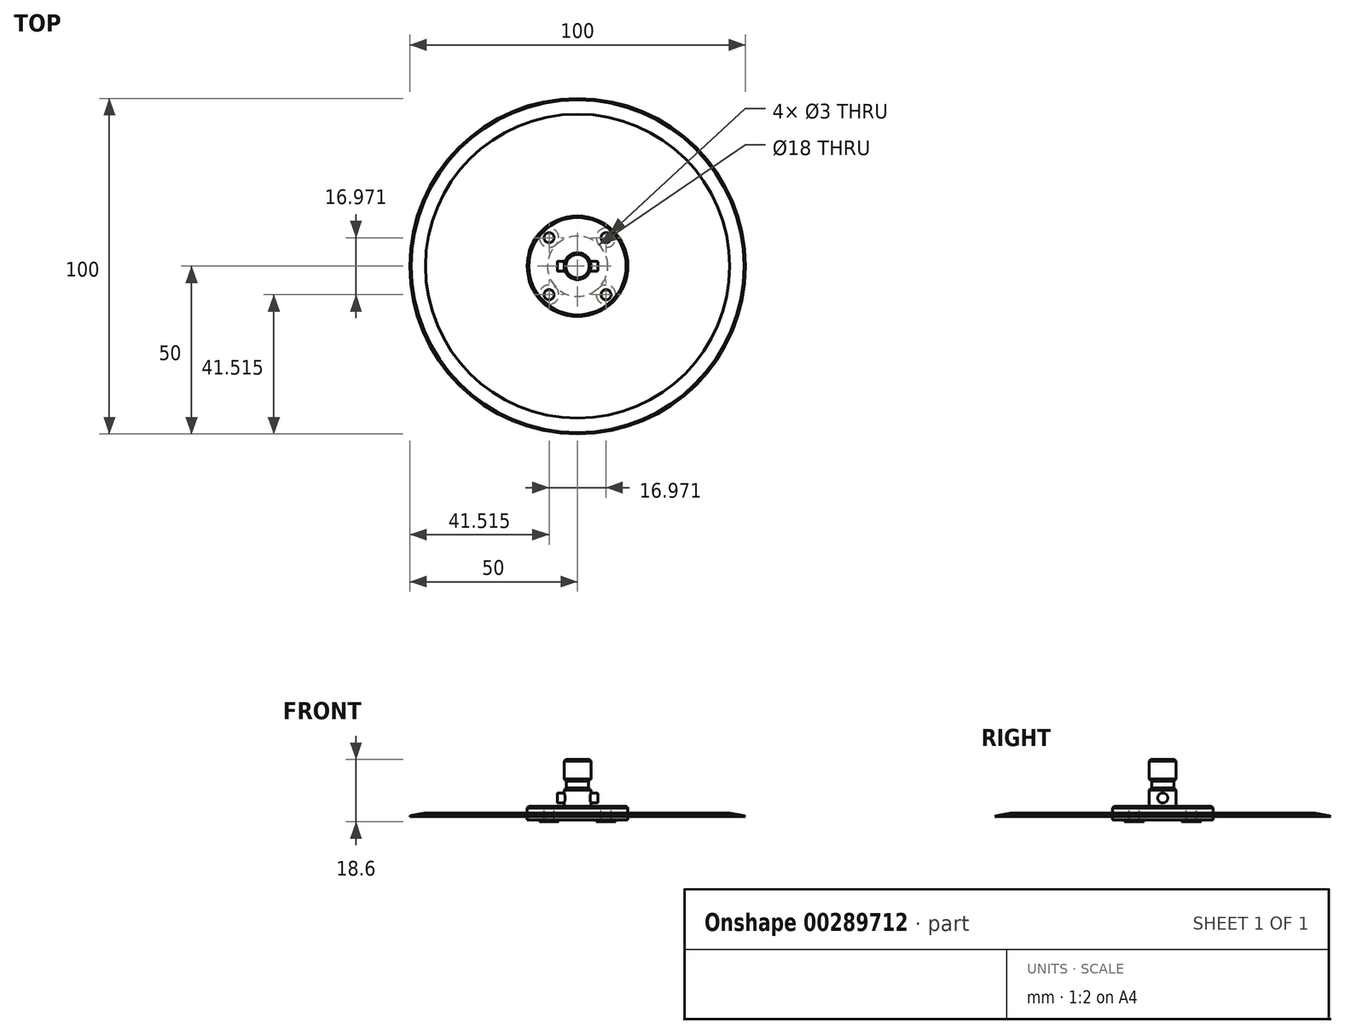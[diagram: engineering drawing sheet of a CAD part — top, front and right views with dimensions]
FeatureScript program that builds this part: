
annotation { "Feature Type Name" : "Feature", "Feature Type Description" : "" }
export const myFeature = defineFeature(function(context is Context, id is Id, definition is map)
    precondition{}
    {
        {
            var Q0;
            Q0=qCreatedBy(makeId("Top.planeOp"),FACE);
            var sketch = newSketch(context, id + "F0", { "sketchPlane" : qUnion([Q0])});
            skCircle(sketch, "E0", {"center": v(0, 0) * mm, "radius": 50 * mm});
            skCircle(sketch, "E1", {"center": v(0, 0) * mm, "radius": 9 * mm});
            skCircle(sketch, "E2", {"center": v(-8.49, -8.49) * mm, "radius": 1.5 * mm});
            skLineSegment(sketch, "E3", {"start": v(0, 0) * mm, "end": v(-8.49, -8.49) * mm, "construction": true});
            skCircle(sketch, "E4.1.0", {"center": v(8.49, -8.49) * mm, "radius": 1.5 * mm});
            skCircle(sketch, "E4.2.0", {"center": v(8.49, 8.49) * mm, "radius": 1.5 * mm});
            skCircle(sketch, "E4.3.0", {"center": v(-8.49, 8.49) * mm, "radius": 1.5 * mm});
            skSolve(sketch);
        }
        {
            var Q0;
            Q0 = qSketchRegion(id + "F0", true);
            var Q1;
            Q1=makeQuery(id+"F0.imprint","IMPRINT",FACE,{"disambiguationData":[TD([[makeQuery(id+"F0.imprint","IMPRINT",EDGE,{"derivedFrom":sQuery(id+"F0.wireOp",EDGE,"E0")}),1.0]])]});
            extrude(context, id + "F1", {"entities" : qUnion([Q0, Q1]), "depth" : 1 * mm});
        }
        {
            var Q0;
            Q0=qCreatedBy(makeId("Front.planeOp"),FACE);
            var sketch = newSketch(context, id + "F2", { "sketchPlane" : qUnion([Q0])});
            skLineSegment(sketch, "E5.0", {"start": v(-50, 0) * mm, "end": v(50, 0) * mm});
            skLineSegment(sketch, "E6", {"start": v(50, 0) * mm, "end": v(49.57, 0.25) * mm});
            skLineSegment(sketch, "E7", {"start": v(49.57, 0.25) * mm, "end": v(39.36, 2.05) * mm});
            skLineSegment(sketch, "E8", {"start": v(39.36, 2.05) * mm, "end": v(52.74, 3.14) * mm});
            skLineSegment(sketch, "E9", {"start": v(52.74, 3.14) * mm, "end": v(50, 0) * mm});
            skLineSegment(sketch, "E10", {"start": v(0, 0) * mm, "end": v(0, -8.1) * mm});
            skSolve(sketch);
        }
        {
            var Q0;
            Q0=makeQuery(id+"F2.imprint","IMPRINT",FACE,{"disambiguationData":[TD([[makeQuery(id+"F2.imprint","IMPRINT",EDGE,{"derivedFrom":sQuery(id+"F2.wireOp",EDGE,"E6")}),-1.0]])]});
            var Q1;
            Q1=sQuery(id+"F2.wireOp",EDGE,"E10");
            revolve(context, id + "F3", {"operationType" : NewBodyOperationType.REMOVE, "entities" : qUnion([Q0]), "axis" : qUnion([Q1]), "revolveType" : RevolveType.FULL, "oppositeDirection" : true});
        }
        {
            var Q0;
            Q0=qCreatedBy(makeId("Front.planeOp"),FACE);
            var sketch = newSketch(context, id + "F4", { "sketchPlane" : qUnion([Q0])});
            skLineSegment(sketch, "E11", {"start": v(0, -0.82) * mm, "end": v(0, -13.84) * mm, "construction": true});
            skLineSegment(sketch, "E12", {"start": v(0, 17) * mm, "end": v(4, 17) * mm});
            skLineSegment(sketch, "E13", {"start": v(4, 17) * mm, "end": v(4, 10.5) * mm});
            skLineSegment(sketch, "E14", {"start": v(4, 10.5) * mm, "end": v(3.3, 10.5) * mm});
            skLineSegment(sketch, "E15", {"start": v(3.3, 10.5) * mm, "end": v(3.3, 8.5) * mm});
            skLineSegment(sketch, "E16", {"start": v(3.3, 8.5) * mm, "end": v(4, 8.5) * mm});
            skLineSegment(sketch, "E17", {"start": v(4, 8.5) * mm, "end": v(4, 3) * mm});
            skLineSegment(sketch, "E18", {"start": v(4, 3) * mm, "end": v(15, 3) * mm});
            skLineSegment(sketch, "E19.0", {"start": v(-45.31, 1) * mm, "end": v(45.31, 1) * mm, "construction": true});
            skLineSegment(sketch, "E20", {"start": v(15, 3) * mm, "end": v(15, 1) * mm});
            skLineSegment(sketch, "E21.0", {"start": v(-9, 1) * mm, "end": v(9, 1) * mm, "construction": true});
            skLineSegment(sketch, "E22", {"start": v(15, 1) * mm, "end": v(9, 1) * mm});
            skLineSegment(sketch, "E23", {"start": v(9, 1) * mm, "end": v(9, 0) * mm});
            skLineSegment(sketch, "E24", {"start": v(9, 0) * mm, "end": v(0, 0) * mm});
            skLineSegment(sketch, "E25", {"start": v(0, 0) * mm, "end": v(0, 17) * mm});
            skSolve(sketch);
        }
        {
            var Q0;
            Q0=makeQuery(id+"F4.imprint","IMPRINT",FACE,{"disambiguationData":[TD([[makeQuery(id+"F4.imprint","IMPRINT",EDGE,{"derivedFrom":sQuery(id+"F4.wireOp",EDGE,"E12")}),-1.0]])]});
            var Q1;
            Q1=sQuery(id+"F4.wireOp",EDGE,"E11");
            revolve(context, id + "F5", {"entities" : qUnion([Q0]), "axis" : qUnion([Q1]), "revolveType" : RevolveType.FULL});
        }
        {
            var Q0;
            Q0=makeQuery(id+"F5.opRevolve","SWEPT_EDGE",EDGE,{"disambiguationData":[OSD([sQuery(id+"F4.wireOp",EDGE,"E12"),sQuery(id+"F4.wireOp",EDGE,"E13")])]});
            var Q1;
            Q1=makeQuery(id+"F5.opRevolve","SWEPT_EDGE",EDGE,{"disambiguationData":[OSD([sQuery(id+"F4.wireOp",EDGE,"E18"),sQuery(id+"F4.wireOp",EDGE,"E20")])]});
            chamfer(context, id + "F6", {"entities" : qUnion([Q0, Q1]), "width" : 0.5 * mm, "tangentPropagation" : true});
        }
        {
            var Q0;
            Q0=makeQuery(id+"F5.opRevolve","SWEPT_EDGE",EDGE,{"disambiguationData":[OSD([sQuery(id+"F4.wireOp",EDGE,"E16"),sQuery(id+"F4.wireOp",EDGE,"E17")])]});
            var Q1;
            Q1=makeQuery(id+"F5.opRevolve","SWEPT_EDGE",EDGE,{"disambiguationData":[OSD([sQuery(id+"F4.wireOp",EDGE,"E13"),sQuery(id+"F4.wireOp",EDGE,"E14")])]});
            chamfer(context, id + "F7", {"entities" : qUnion([Q0, Q1]), "width" : 0.7 * mm, "tangentPropagation" : true});
        }
        {
            var Q0;
            Q0=makeQuery(id+"F1.opExtrude","CAP_FACE",FACE,{"disambiguationData":[OSD([sQuery(id+"F0.wireOp",EDGE,"E0"),sQuery(id+"F0.wireOp",EDGE,"E1"),sQuery(id+"F0.wireOp",EDGE,"E2"),sQuery(id+"F0.wireOp",EDGE,"E4.1.0"),sQuery(id+"F0.wireOp",EDGE,"E4.2.0"),sQuery(id+"F0.wireOp",EDGE,"E4.3.0")])],"isStart":true});
            var sketch = newSketch(context, id + "F8", { "sketchPlane" : qUnion([Q0])});
            skCircle(sketch, "E26", {"center": v(0, 0) * mm, "radius": 15 * mm});
            skSolve(sketch);
        }
        {
            var Q0;
            Q0 = qSketchRegion(id + "F8", true);
            extrude(context, id + "F9", {"entities" : qUnion([Q0]), "depth" : 1.1 * mm});
        }
        {
            var Q0;
            Q0=qCreatedBy(makeId("Front.planeOp"),FACE);
            var sketch = newSketch(context, id + "F10", { "sketchPlane" : qUnion([Q0])});
            skLineSegment(sketch, "E27", {"start": v(0, 0) * mm, "end": v(0, 41.1) * mm});
            skSolve(sketch);
        }
        {
            var Q0;
            Q0=qCreatedBy(makeId("Front.planeOp"),FACE);
            var Q1;
            Q1=sQuery(id+"F10.wireOp",EDGE,"E27");
            cPlane(context, id + "F11", {"entities" : qUnion([Q0, Q1]), "cplaneType" : CPlaneType.LINE_ANGLE, "offset" : 25 * mm, "angle" : 45 * degree, "width" : 150 * mm, "height" : 150 * mm});
        }
        {
            var Q0;
            Q0=qCreatedBy(id+"F11.planeOp",FACE);
            var sketch = newSketch(context, id + "F12", { "sketchPlane" : qUnion([Q0])});
            skLineSegment(sketch, "E28.0", {"start": v(-13.5, 0) * mm, "end": v(-10.5, 0) * mm});
            skLineSegment(sketch, "E29.0.0", {"start": v(15, -1.1) * mm, "end": v(-15, -1.1) * mm});
            skLineSegment(sketch, "E30.0.0", {"start": v(-14.5, 3) * mm, "end": v(14.5, 3) * mm});
            skLineSegment(sketch, "E31", {"start": v(-12, 4.8) * mm, "end": v(-12, -5.4) * mm, "construction": true});
            skPoint(sketch, "E31.startSnap0", {"position": v(-12, 0) * mm});
            skLineSegment(sketch, "E32", {"start": v(-12, -1.6) * mm, "end": v(-14.9, -1.6) * mm});
            skLineSegment(sketch, "E33", {"start": v(-14.9, -1.6) * mm, "end": v(-14.9, -1.1) * mm});
            skLineSegment(sketch, "E34", {"start": v(-14.9, -1.1) * mm, "end": v(-13.5, -1.1) * mm});
            skLineSegment(sketch, "E35", {"start": v(-13.5, -1.1) * mm, "end": v(-13.5, 3) * mm});
            skLineSegment(sketch, "E36", {"start": v(-13.5, 3) * mm, "end": v(-14.14, 3) * mm});
            skFitSpline(sketch, "E37", {"points": [v(-14.14, 3) * mm, v(-13.63, 3.33) * mm, v(-12.85, 3.46) * mm, v(-12, 3.48) * mm], "startDerivative": vector(1.57, 1.26) * mm, "endDerivative": vector(2.37, 0.01) * mm});
            skLineSegment(sketch, "E38", {"start": v(-12, 3.48) * mm, "end": v(-12, -1.6) * mm});
            skSolve(sketch);
        }
        {
            var Q0;
            {var subQ0=sQuery(id+"F12.wireOp",EDGE,"E36");Q0=makeQuery(id+"F12.imprint","IMPRINT",FACE,{"disambiguationData":[TD([[makeQuery(id+"F12.imprint","IMPRINT",EDGE,{"derivedFrom":subQ0}),-1.0]])]});}
            var Q1;
            {var subQ0=sQuery(id+"F12.wireOp",EDGE,"E35");var subQ1=sQuery(id+"F12.wireOp",EDGE,"E28.0");var subQ2=makeQuery(id+"F12.imprint","INTERSECT",VERTEX,{"derivedFrom":[subQ1,subQ0]});Q1=makeQuery(id+"F12.imprint","IMPRINT",FACE,{"disambiguationData":[TD([[makeQuery(id+"F12.imprint","IMPRINT",EDGE,{"disambiguationData":[TD([[subQ2,-1.0]])],"derivedFrom":subQ1}),1.0]])]});}
            var Q2;
            {var subQ1=sQuery(id+"F12.wireOp",EDGE,"E32");Q2=makeQuery(id+"F12.imprint","IMPRINT",FACE,{"disambiguationData":[TD([[makeQuery(id+"F12.imprint","IMPRINT",EDGE,{"derivedFrom":subQ1}),-1.0]])]});}
            var Q3;
            {var subQ0=sQuery(id+"F12.wireOp",EDGE,"E35");var subQ1=sQuery(id+"F12.wireOp",EDGE,"E28.0");var subQ2=makeQuery(id+"F12.imprint","INTERSECT",VERTEX,{"derivedFrom":[subQ1,subQ0]});Q3=makeQuery(id+"F12.imprint","IMPRINT",FACE,{"disambiguationData":[TD([[makeQuery(id+"F12.imprint","IMPRINT",EDGE,{"disambiguationData":[TD([[subQ2,-1.0]])],"derivedFrom":subQ1}),-1.0]])]});}
            var Q4;
            Q4=sQuery(id+"F12.wireOp",EDGE,"E31");
            revolve(context, id + "F13", {"entities" : qUnion([Q0, Q1, Q2, Q3]), "axis" : qUnion([Q4]), "revolveType" : RevolveType.FULL});
        }
        {
            var Q0;
            Q0=makeQuery(id+"F13.opRevolve","SWEPT_BODY",BODY,{"disambiguationData":[OSD([sQuery(id+"F12.wireOp",EDGE,"E32"),sQuery(id+"F12.wireOp",EDGE,"E33"),sQuery(id+"F12.wireOp",EDGE,"E34"),sQuery(id+"F12.wireOp",EDGE,"E35"),sQuery(id+"F12.wireOp",EDGE,"E36"),sQuery(id+"F12.wireOp",EDGE,"E37"),sQuery(id+"F12.wireOp",EDGE,"E38")])]});
            var Q1;
            Q1=sQuery(id+"F10.wireOp",EDGE,"E27");
            circularPattern(context, id + "F14", {"entities" : qUnion([Q0]), "axis" : qUnion([Q1]), "angle" : 360 * degree, "instanceCount" : 4, "equalSpace" : true});
        }
        {
            var Q0;
            Q0=qCreatedBy(makeId("Right.planeOp"),FACE);
            var sketch = newSketch(context, id + "F15", { "sketchPlane" : qUnion([Q0])});
            skLineSegment(sketch, "E39.0", {"start": v(-3.5, 17) * mm, "end": v(3.5, 17) * mm, "construction": true});
            skCircle(sketch, "E40", {"center": v(0, 5.5) * mm, "radius": 1.5 * mm});
            skPoint(sketch, "E40.centerSnap0", {"position": v(0, 17) * mm});
            skSolve(sketch);
        }
        {
            var Q0;
            Q0=makeQuery(id+"F15.imprint","IMPRINT",FACE,{"disambiguationData":[TD([[makeQuery(id+"F15.imprint","IMPRINT",EDGE,{"derivedFrom":sQuery(id+"F15.wireOp",EDGE,"E40")}),1.0]])]});
            var Q1;
            Q1=sQuery(id+"F15.wireOp",EDGE,"E39.0");
            var Q2;
            Q2=sQuery(id+"F15.wireOp",EDGE,"E40");
            extrude(context, id + "F16", {"entities" : qUnion([Q0]), "operationType" : NewBodyOperationType.ADD, "surfaceEntities" : qUnion([Q1, Q2]), "endBound" : BoundingType.SYMMETRIC, "depth" : 12 * mm});
        }
        {
            var Q0;
            Q0=makeQuery(id+"F16.opExtrude","CAP_EDGE",EDGE,{"disambiguationData":[OSD([sQuery(id+"F15.wireOp",EDGE,"E40")])],"isStart":true});
            var Q1;
            Q1=makeQuery(id+"F16.opExtrude","CAP_EDGE",EDGE,{"disambiguationData":[OSD([sQuery(id+"F15.wireOp",EDGE,"E40")])],"isStart":false});
            fillet(context, id + "F17", {"entities" : qUnion([Q0, Q1]), "radius" : 0.2 * mm, "tangentPropagation" : true, "allowEdgeOverflow" : false});
        }
    });
